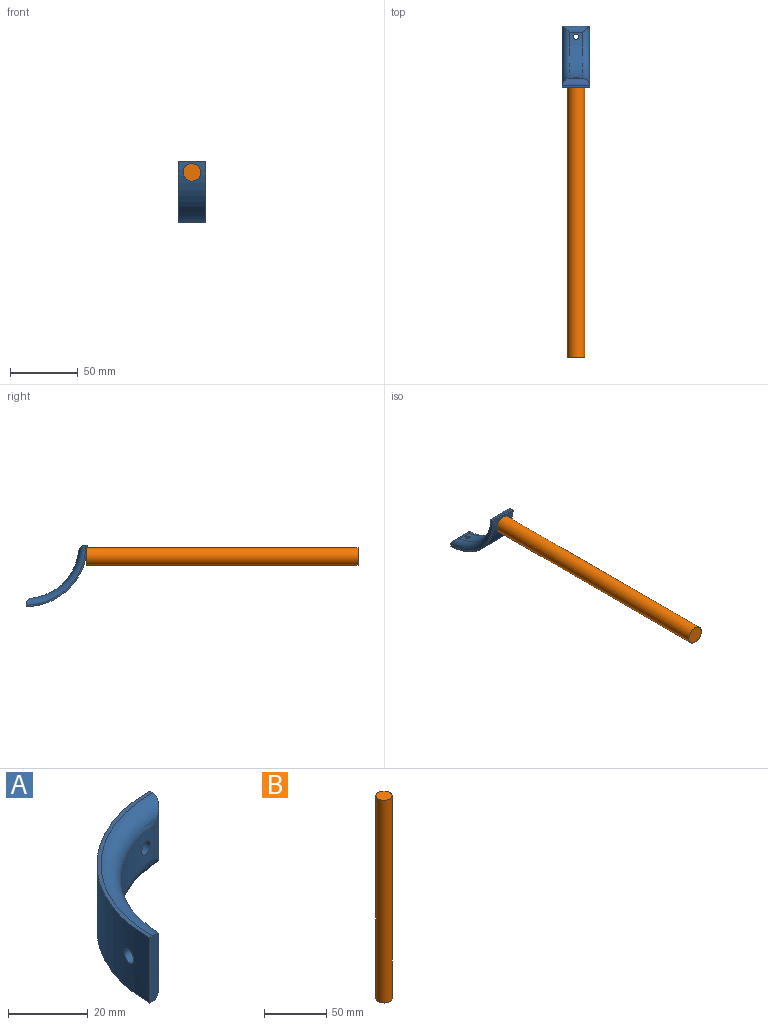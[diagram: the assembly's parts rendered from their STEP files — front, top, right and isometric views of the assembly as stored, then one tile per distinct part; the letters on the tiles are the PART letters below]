
ASSEMBLY  parts=2 mates=1
PART A: 12 faces, bbox 51.5x51.5x20 mm
  f0: plane 20x1.29mm, normal (1,0,0), area 25.7mm2, adj f1,f4,f5,f8,f9,f10
  f1: cylinder r=45mm len=45mm, axis (0,0,-1), area 1388.2mm2, adj f0,f2,f4,f5,f6,f7
  f2: plane 20x1.29mm, normal (0,-1,0), area 25.7mm2, adj f1,f4,f5,f9,f10,f11
  f3: cylinder r=39mm len=34.32mm, axis (0,0,-1), area 498.1mm2, adj f6,f7,f8,f9,f10,f11
  f4: plane 45x45mm, normal (0,0,1), area 69.9mm2, adj f0,f1,f2,f9
  f5: plane 45x45mm, normal (0,0,-1), area 69.9mm2, adj f0,f1,f2,f10
  f6: cylinder r=2mm len=6.9mm, axis (0,-1,0), area 76.9mm2, adj f1,f3
  f7: cylinder r=2mm len=6.9mm, axis (1,0,0), area 76.9mm2, adj f1,f3
  f8: cylinder r=5mm len=19.98mm, axis (0,0,-1), area 118.6mm2, adj f0,f3,f9,f10
  f9: torus R=44mm, axis (0,0,1), area 479.1mm2, adj f0,f2,f3,f4,f8,f11
  f10: torus R=44mm, axis (0,0,1), area 479.1mm2, adj f0,f2,f3,f5,f8,f11
  f11: cylinder r=5mm len=19.98mm, axis (0,0,-1), area 118.6mm2, adj f2,f3,f9,f10
PART B: 3 faces, bbox 13x13x200 mm
  f0: cylinder r=6.5mm len=200mm, axis (0,0,-1), area 8168.1mm2, adj f1,f2
  f1: plane 13x13mm, normal (0,0,1), area 132.7mm2, adj f0
  f2: plane 13x13mm, normal (0,0,-1), area 132.7mm2, adj f0
PLACE A rot(axis=(-0.58,-0.58,0.58),120deg) t=(44.06,79.85,17.41)mm
PLACE B rot(axis=(-1,0,0),90deg) t=(1,-164.79,31.41)mm
MATE fastened A.f7 <-> B.f0  axis (0,1,0) through (34.06,35.21,9.41)mm
